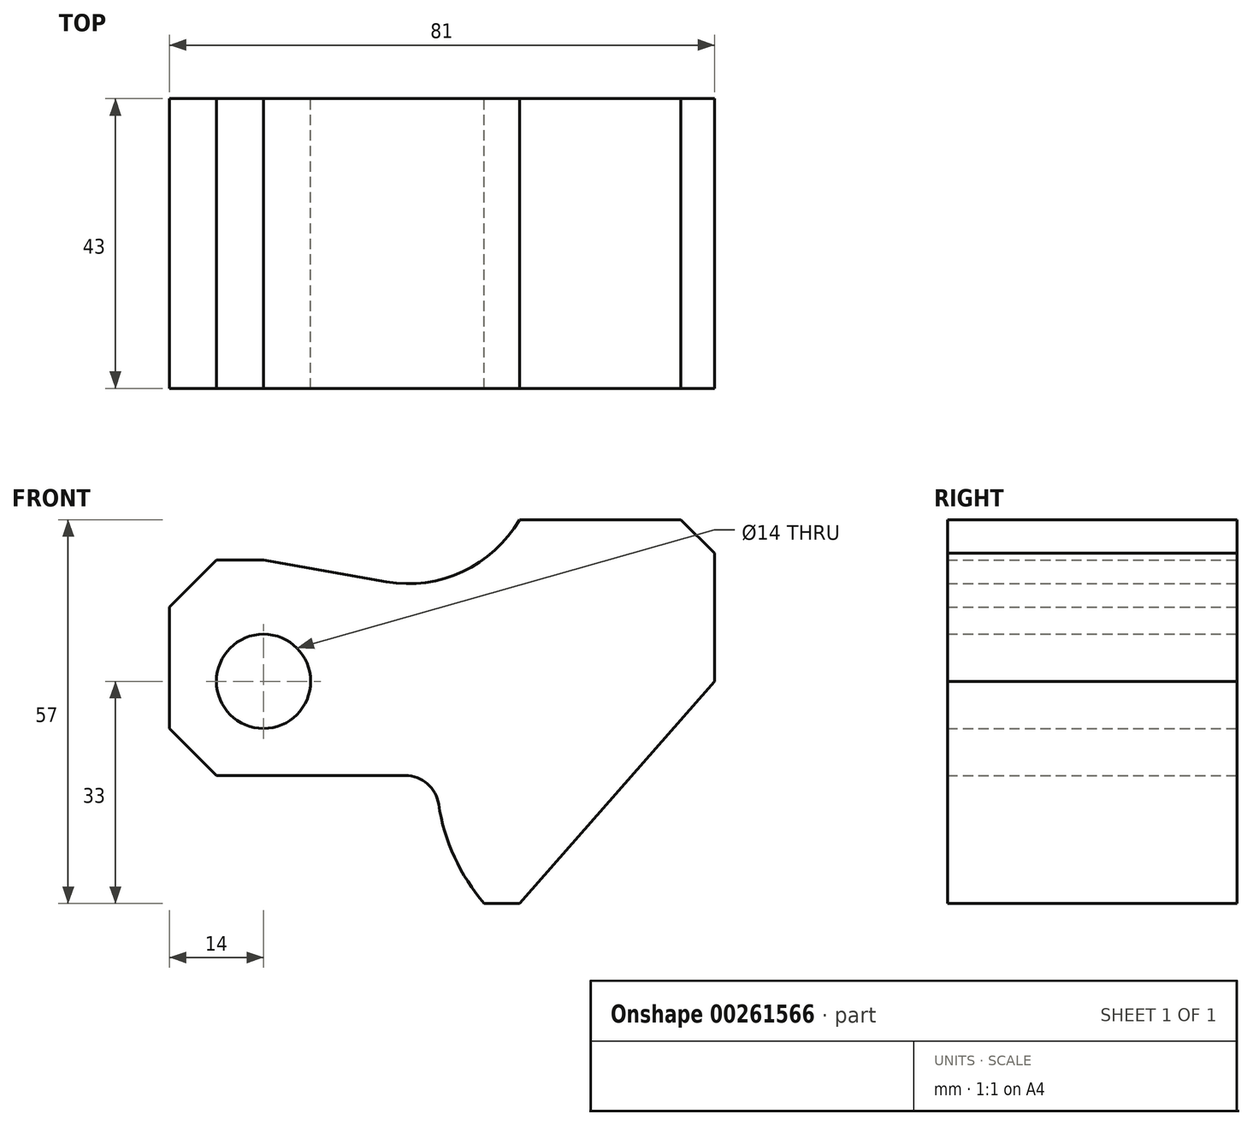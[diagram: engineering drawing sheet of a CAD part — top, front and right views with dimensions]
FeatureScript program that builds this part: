
annotation { "Feature Type Name" : "Feature", "Feature Type Description" : "" }
export const myFeature = defineFeature(function(context is Context, id is Id, definition is map)
    precondition{}
    {
        {
            var Q0;
            Q0=qCreatedBy(makeId("Front.planeOp"),FACE);
            var sketch = newSketch(context, id + "F0", { "sketchPlane" : qUnion([Q0])});
            skLineSegment(sketch, "E0.bottom", {"start": v(40.5, 28.5) * mm, "end": v(-40.5, 28.5) * mm, "construction": true});
            skLineSegment(sketch, "E0.top", {"start": v(40.5, -28.5) * mm, "end": v(-40.5, -28.5) * mm, "construction": true});
            skLineSegment(sketch, "E0.left", {"start": v(40.5, 28.5) * mm, "end": v(40.5, -28.5) * mm, "construction": true});
            skLineSegment(sketch, "E0.right", {"start": v(-40.5, 28.5) * mm, "end": v(-40.5, -28.5) * mm, "construction": true});
            skPoint(sketch, "E0.middle", {"position": v(0, 0) * mm});
            skLineSegment(sketch, "E1", {"start": v(35.5, 28.5) * mm, "end": v(40.5, 23.5) * mm});
            skLineSegment(sketch, "E2", {"start": v(35.5, 28.5) * mm, "end": v(11.5, 28.5) * mm});
            skLineSegment(sketch, "E3", {"start": v(40.5, 23.5) * mm, "end": v(40.5, 4.5) * mm});
            skLineSegment(sketch, "E4", {"start": v(40.5, 4.5) * mm, "end": v(11.5, -28.5) * mm});
            skLineSegment(sketch, "E5", {"start": v(11.5, -28.5) * mm, "end": v(6.29, -28.5) * mm});
            skArc(sketch, "E6", {"start": v(-0.49, -13.76) * mm, "mid": v(1.85, -21.62) * mm, "end": v(6.29, -28.5) * mm});
            skLineSegment(sketch, "E7", {"start": v(-5.43, -9.5) * mm, "end": v(-33.5, -9.5) * mm});
            skLineSegment(sketch, "E8", {"start": v(-33.5, -9.5) * mm, "end": v(-40.5, -2.5) * mm});
            skArc(sketch, "E9", {"start": v(-8.26, 19.28) * mm, "mid": v(3.07, 20.78) * mm, "end": v(11.5, 28.5) * mm});
            skLineSegment(sketch, "E10", {"start": v(-8.26, 19.28) * mm, "end": v(-26.5, 22.5) * mm});
            skLineSegment(sketch, "E11", {"start": v(-40.5, -2.5) * mm, "end": v(-40.5, 15.5) * mm});
            skLineSegment(sketch, "E12", {"start": v(-40.5, 15.5) * mm, "end": v(-33.5, 22.5) * mm});
            skLineSegment(sketch, "E13", {"start": v(-33.5, 22.5) * mm, "end": v(-26.5, 22.5) * mm});
            skCircle(sketch, "E14", {"center": v(-26.5, 4.5) * mm, "radius": 7 * mm});
            skArc(sketch, "E15", {"start": v(-0.49, -13.76) * mm, "mid": v(-2.17, -10.71) * mm, "end": v(-5.43, -9.5) * mm});
            skSolve(sketch);
        }
        {
            var Q0;
            Q0=makeQuery(id+"F0.imprint","IMPRINT",FACE,{"disambiguationData":[TD([[makeQuery(id+"F0.imprint","IMPRINT",EDGE,{"derivedFrom":sQuery(id+"F0.wireOp",EDGE,"E1")}),-1.0]])]});
            extrude(context, id + "F1", {"entities" : qUnion([Q0]), "depth" : 43 * mm, "symmetric" : true});
        }
    });
